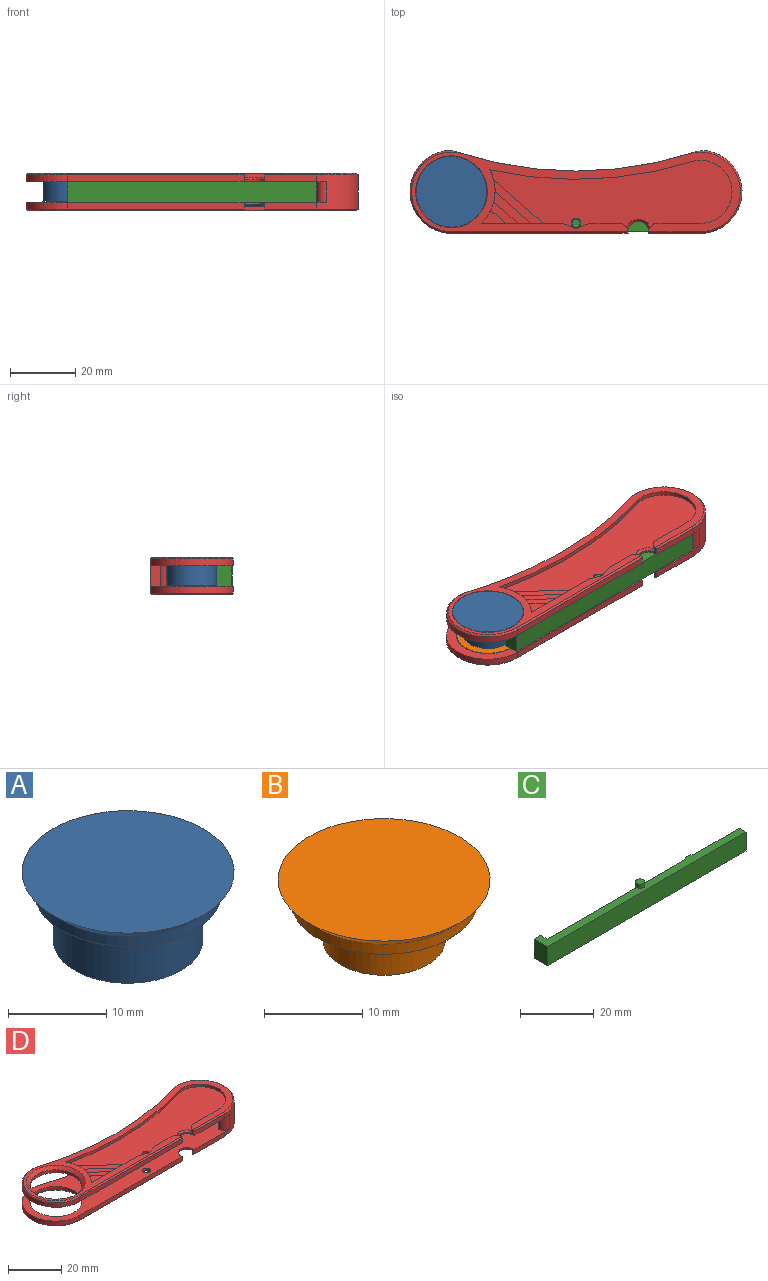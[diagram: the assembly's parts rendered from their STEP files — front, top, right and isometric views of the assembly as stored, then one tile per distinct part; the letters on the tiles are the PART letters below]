
ASSEMBLY  parts=4 mates=3
PART A: 8 faces, bbox 21.6x21.6x8.5 mm
  f0: cylinder r=6.35mm len=12.7mm, axis (0,0,1), area 237.1mm2, adj f4,f5
  f1: cylinder r=9.53mm len=19.05mm, axis (0,0,1), area 76mm2, adj f2,f6
  f2: plane 19.05x19.05mm, normal (0,0,-1), area 102.6mm2, adj f1,f3
  f3: cylinder r=7.62mm len=15.24mm, axis (0,0,1), area 284.6mm2, adj f2,f4
  f4: plane 15.24x15.24mm, normal (0,0,-1), area 55.7mm2, adj f0,f3
  f5: plane 12.7x12.7mm, normal (0,0,-1), area 126.7mm2, adj f0
  f6: cone r=9.53mm half-angle=45deg, axis (0,0,1), area 114.7mm2, adj f1,f7
  f7: plane 21.59x21.59mm, normal (0,0,1), area 366.1mm2, adj f6
PART B: 6 faces, bbox 21.6x21.6x7.5 mm
  f0: cylinder r=9.53mm len=19.05mm, axis (0,0,1), area 76mm2, adj f1,f4
  f1: plane 19.05x19.05mm, normal (0,0,-1), area 163.4mm2, adj f0,f2
  f2: cylinder r=6.22mm len=12.45mm, axis (0,0,1), area 193.7mm2, adj f1,f3
  f3: plane 12.45x12.45mm, normal (0,0,-1), area 121.7mm2, adj f2
  f4: cone r=9.53mm half-angle=45deg, axis (0,0,1), area 114.7mm2, adj f0,f5
  f5: plane 21.59x21.59mm, normal (0,0,1), area 366.1mm2, adj f4
PART C: 14 faces, bbox 76.2x5.1x8.9 mm
  f0: plane 76.2x5.08mm, normal (0,0,1), area 199.1mm2, adj f2,f3,f4,f5,f6,f7,f8,f9
  f1: plane 76.2x5.08mm, normal (0,0,-1), area 199.1mm2, adj f2,f3,f4,f5,f6,f7,f8,f9
  f2: plane 17.15x6.3mm, normal (0,1,0), area 108mm2, adj f0,f1,f3,f11
  f3: cylinder r=3.17mm len=6.3mm, axis (0,0,-1), area 25.7mm2, adj f0,f1,f2,f4
  f4: plane 15.88x6.3mm, normal (0,1,0), area 100mm2, adj f0,f1,f3,f5
  f5: cylinder r=1.27mm len=8.89mm, axis (0,0,-1), area 45.8mm2, adj f0,f1,f4,f6,f12,f13
  f6: plane 34.29x6.3mm, normal (0,1,0), area 216mm2, adj f0,f1,f5,f7
  f7: plane 6.3x2.54mm, normal (1,0,0), area 16mm2, adj f0,f1,f6,f8
  f8: plane 6.3x2.54mm, normal (0,1,0), area 16mm2, adj f0,f1,f7,f9
  f9: plane 6.3x5.08mm, normal (-1,0,0), area 32mm2, adj f0,f1,f8,f10
  f10: plane 76.2x6.3mm, normal (0,-1,0), area 480mm2, adj f0,f1,f9,f11
  f11: plane 6.3x2.54mm, normal (1,0,0), area 16mm2, adj f0,f1,f2,f10
  f12: plane 2.54x2.54mm, normal (0,0,-1), area 5.1mm2, adj f5
  f13: plane 2.54x2.54mm, normal (0,0,1), area 5.1mm2, adj f5
PART D: 78 faces, bbox 101.7x25.5x11.5 mm
  f0: plane 54.02x2.03mm, normal (0,-1,0), area 109.8mm2, adj f10,f18,f31,f64
  f1: plane 100.58x24.38mm, normal (0,0,-1), area 521.2mm2, adj f4,f7,f8,f16,f24,f30,f31,f32
  f2: plane 54.02x2.03mm, normal (0,-1,0), area 109.8mm2, adj f13,f23,f28,f66
  f3: plane 15.92x0.51mm, normal (0,-0.71,0.71), area 11.4mm2, adj f12,f14,f27,f66
  f4: plane 15.92x0.51mm, normal (0,-0.71,-0.71), area 11.4mm2, adj f1,f9,f30,f64
  f5: plane 10.04x1.27mm, normal (0,1,0), area 12.7mm2, adj f12,f47,f72,f76
  f6: plane 24.8x1.27mm, normal (0,1,0), area 18.1mm2, adj f12,f36,f38,f39,f40,f41,f42,f43
  f7: plane 14.21x1.27mm, normal (0,1,0), area 18mm2, adj f1,f52,f54,f69
  f8: plane 10.44x1.27mm, normal (0,1,0), area 13.3mm2, adj f1,f54,f70,f73
  f9: plane 15.92x2.03mm, normal (0,-1,0), area 32.3mm2, adj f4,f15,f18,f64
  f10: cylinder r=12.7mm len=25.17mm, axis (0,0,-1), area 76.1mm2, adj f0,f18,f32,f35
  f11: cylinder r=9.73mm len=19.46mm, axis (0,0,-1), area 77.6mm2, adj f18,f24
  f12: plane 100.6x24.4mm, normal (0,0,1), area 524.8mm2, adj f3,f5,f6,f21,f25,f26,f27,f28
  f13: cylinder r=12.7mm len=25.17mm, axis (0,0,-1), area 76.1mm2, adj f2,f23,f29,f34
  f14: plane 15.92x2.03mm, normal (0,-1,0), area 32.3mm2, adj f3,f15,f23,f66
  f15: cylinder r=12.7mm len=25.17mm, axis (0,0,-1), area 369.8mm2, adj f9,f14,f18,f23,f27,f30,f33,f77
  f16: cylinder r=117.47mm len=73.38mm, axis (0,0,-1), area 189.5mm2, adj f1,f18,f30,f32,f33,f35
  f17: cylinder r=9.73mm len=10.94mm, axis (0,0,-1), area 21mm2, adj f22,f23,f26
  f18: plane 98.55x25.31mm, normal (0,0,1), area 1688.9mm2, adj f0,f9,f10,f11,f15,f16,f19,f20
  f19: cylinder r=9.65mm len=19.3mm, axis (0,0,-1), area 192.5mm2, adj f18,f20,f23,f62
  f20: plane 6.35x2.89mm, normal (-1,0,0), area 18.4mm2, adj f18,f19,f23,f33
  f21: cylinder r=117.47mm len=73.38mm, axis (0,0,-1), area 189.5mm2, adj f12,f23,f27,f29,f33,f34
  f22: extruded ~19.46x19.38mm, area 56.7mm2, adj f17,f23,f25
  f23: plane 98.55x25.31mm, normal (0,0,-1), area 1688.8mm2, adj f2,f13,f14,f15,f17,f19,f20,f21
  f24: cone r=11mm half-angle=45deg, axis (0,0,-1), area 116.9mm2, adj f1,f11
  f25: bspline ~22.01x21.95mm, area 85.4mm2, adj f12,f22,f26
  f26: cone r=9.73mm half-angle=45deg, axis (0,0,1), area 31.6mm2, adj f12,f17,f25
  f27: cone r=12.19mm half-angle=45deg, axis (0,0,-1), area 28.1mm2, adj f3,f12,f15,f21,f33
  f28: plane 54.02x0.51mm, normal (0,-0.71,0.71), area 38.8mm2, adj f2,f12,f29,f66
  f29: cone r=12.7mm half-angle=45deg, axis (0,0,-1), area 28.1mm2, adj f12,f13,f21,f28,f34
  f30: cone r=12.7mm half-angle=45deg, axis (0,0,1), area 28.1mm2, adj f1,f4,f15,f16,f33
  f31: plane 54.02x0.51mm, normal (0,-0.71,-0.71), area 38.8mm2, adj f0,f1,f32,f64
  f32: cone r=12.19mm half-angle=45deg, axis (0,0,1), area 28.1mm2, adj f1,f10,f16,f31,f35
  f33: cylinder r=7.62mm len=11.2mm, axis (0,0,1), area 32.7mm2, adj f15,f16,f18,f20,f21,f23,f27,f30
  f34: cylinder r=7.62mm len=3.83mm, axis (0,0,1), area 8.6mm2, adj f13,f21,f23,f29
  f35: cylinder r=7.62mm len=3.83mm, axis (0,0,1), area 8.6mm2, adj f10,f16,f18,f32
  f36: cylinder r=13.65mm len=16.41mm, axis (0,0,1), area 13mm2, adj f6,f12,f38,f39,f40,f41,f42,f43
  f37: plane 14.26x1.27mm, normal (0,1,0), area 18.1mm2, adj f12,f47,f48,f71
  f38: plane 7.47x4.03mm, normal (0,0,1), area 14.3mm2, adj f6,f36,f39
  f39: plane 4.54x4.03mm, normal (0.66,0.75,0), area 1.5mm2, adj f6,f36,f38,f40
  f40: plane 8.37x6.61mm, normal (0,0,1), area 20.2mm2, adj f6,f36,f39,f41
  f41: plane 7.44x6.61mm, normal (0.66,0.75,0), area 2.5mm2, adj f6,f36,f40,f42
  f42: plane 11.27x9.65mm, normal (0,0,1), area 30.9mm2, adj f6,f36,f41,f43
  f43: plane 10.87x9.65mm, normal (0.66,0.75,0), area 3.7mm2, adj f6,f36,f42,f44
  f44: plane 15.17x13.47mm, normal (0,0,1), area 43.9mm2, adj f6,f36,f43,f45
  f45: plane 15.17x13.47mm, normal (0.66,0.75,0), area 5.2mm2, adj f6,f36,f44,f47
  f46: cylinder r=120.02mm len=63.06mm, axis (0,0,1), area 81.1mm2, adj f12,f36,f47,f48
  f47: plane 74.17x20.69mm, normal (0,0,1), area 995.3mm2, adj f5,f6,f36,f37,f45,f46,f48,f65
  f48: cylinder r=9.65mm len=19.3mm, axis (0,0,1), area 40.4mm2, adj f12,f37,f46,f47
  f49: plane 15.78x14.01mm, normal (0.66,0.75,0), area 5.4mm2, adj f50,f53,f54,f56
  f50: cylinder r=13.65mm len=16.9mm, axis (0,0,-1), area 12.9mm2, adj f1,f49,f51,f53,f54,f55,f56,f57
  f51: cylinder r=120.02mm len=61.1mm, axis (0,0,-1), area 78.5mm2, adj f1,f50,f52,f54
  f52: cylinder r=9.65mm len=19.3mm, axis (0,0,-1), area 40.4mm2, adj f1,f7,f51,f54
  f53: plane 25.25x1.27mm, normal (0,1,0), area 16.3mm2, adj f1,f49,f50,f54,f55,f56,f57,f58
  f54: plane 72.22x20.57mm, normal (0,0,-1), area 982mm2, adj f7,f8,f49,f50,f51,f52,f53,f63
  f55: plane 11.68x10.37mm, normal (0.66,0.75,0), area 4mm2, adj f50,f53,f56,f58
  f56: plane 15.78x14.01mm, normal (0,0,-1), area 46.3mm2, adj f49,f50,f53,f55
  f57: plane 8.36x7.42mm, normal (0.66,0.75,0), area 2.8mm2, adj f50,f53,f58,f60
  f58: plane 12.18x10.37mm, normal (0,0,-1), area 33.9mm2, adj f50,f53,f55,f57
  f59: plane 5.53x4.91mm, normal (0.66,0.75,0), area 1.9mm2, adj f50,f53,f60,f61
  f60: plane 9.35x7.42mm, normal (0,0,-1), area 23.5mm2, adj f50,f53,f57,f59
  f61: plane 9.81x4.91mm, normal (0,0,-1), area 22.4mm2, adj f50,f53,f59
  f62: plane 6.35x0.19mm, normal (-1,0,0), area 1.2mm2, adj f18,f19,f23,f77
  f63: cylinder r=1.52mm len=3.05mm, axis (0,0,-1), area 14.5mm2, adj f1,f18,f54,f73,f74
  f64: cylinder r=3.17mm len=6.35mm, axis (0,0,-1), area 9.9mm2, adj f0,f1,f4,f9,f18,f31,f67,f69
  f65: cylinder r=1.52mm len=3.05mm, axis (0,0,-1), area 14.8mm2, adj f12,f23,f47,f75,f76
  f66: cylinder r=3.17mm len=6.35mm, axis (0,0,-1), area 10.8mm2, adj f2,f3,f12,f14,f23,f28,f68,f71
  f67: cone r=3.17mm half-angle=45deg, axis (0,0,-1), area 8.7mm2, adj f54,f64,f69,f70
  f68: cone r=3.17mm half-angle=45deg, axis (0,0,1), area 8.3mm2, adj f47,f66,f71,f72
  f69: plane 1.96x1.92mm, normal (-0.74,0.67,0), area 3.5mm2, adj f1,f7,f54,f64,f67
  f70: plane 1.96x1.92mm, normal (0.74,0.67,0), area 3.5mm2, adj f1,f8,f54,f64,f67
  f71: plane 2.04x1.95mm, normal (-0.77,0.64,0), area 3.5mm2, adj f12,f37,f47,f66,f68
  f72: plane 2.04x1.95mm, normal (0.77,0.64,0), area 3.5mm2, adj f5,f12,f47,f66,f68
  f73: plane 2.9x1.27mm, normal (-0.3,0.95,0), area 3.9mm2, adj f1,f8,f54,f63
  f74: plane 2.9x1.27mm, normal (0.3,0.95,0), area 3.9mm2, adj f1,f53,f54,f63
  f75: plane 3.25x1.27mm, normal (0.34,0.94,0), area 4.4mm2, adj f6,f12,f47,f65
  f76: plane 3.25x1.27mm, normal (-0.34,0.94,0), area 4.4mm2, adj f5,f12,f47,f65
  f77: cylinder r=2.54mm len=6.35mm, axis (0,0,-1), area 29.4mm2, adj f15,f18,f23,f62
PLACE A t=(-38.38,0.87,5.93)mm
PLACE B rot(axis=(1,0,0),180deg) t=(12.42,0.87,-2.96)mm
PLACE C t=(-0.28,-11.32,-1.69)mm
PLACE D t=(-0.28,0.87,-4.23)mm fixed
MATE revolute C.f5 <-> D.f63  axis (0,0,1) through (-0.28,-8.78,5.93)mm
MATE fastened B.f0 <-> D.f11  axis (0,0,-1) through (-38.38,0.87,-2.96)mm
MATE fastened A.f1 <-> D.f11  axis (0,0,1) through (-38.38,0.87,5.93)mm
